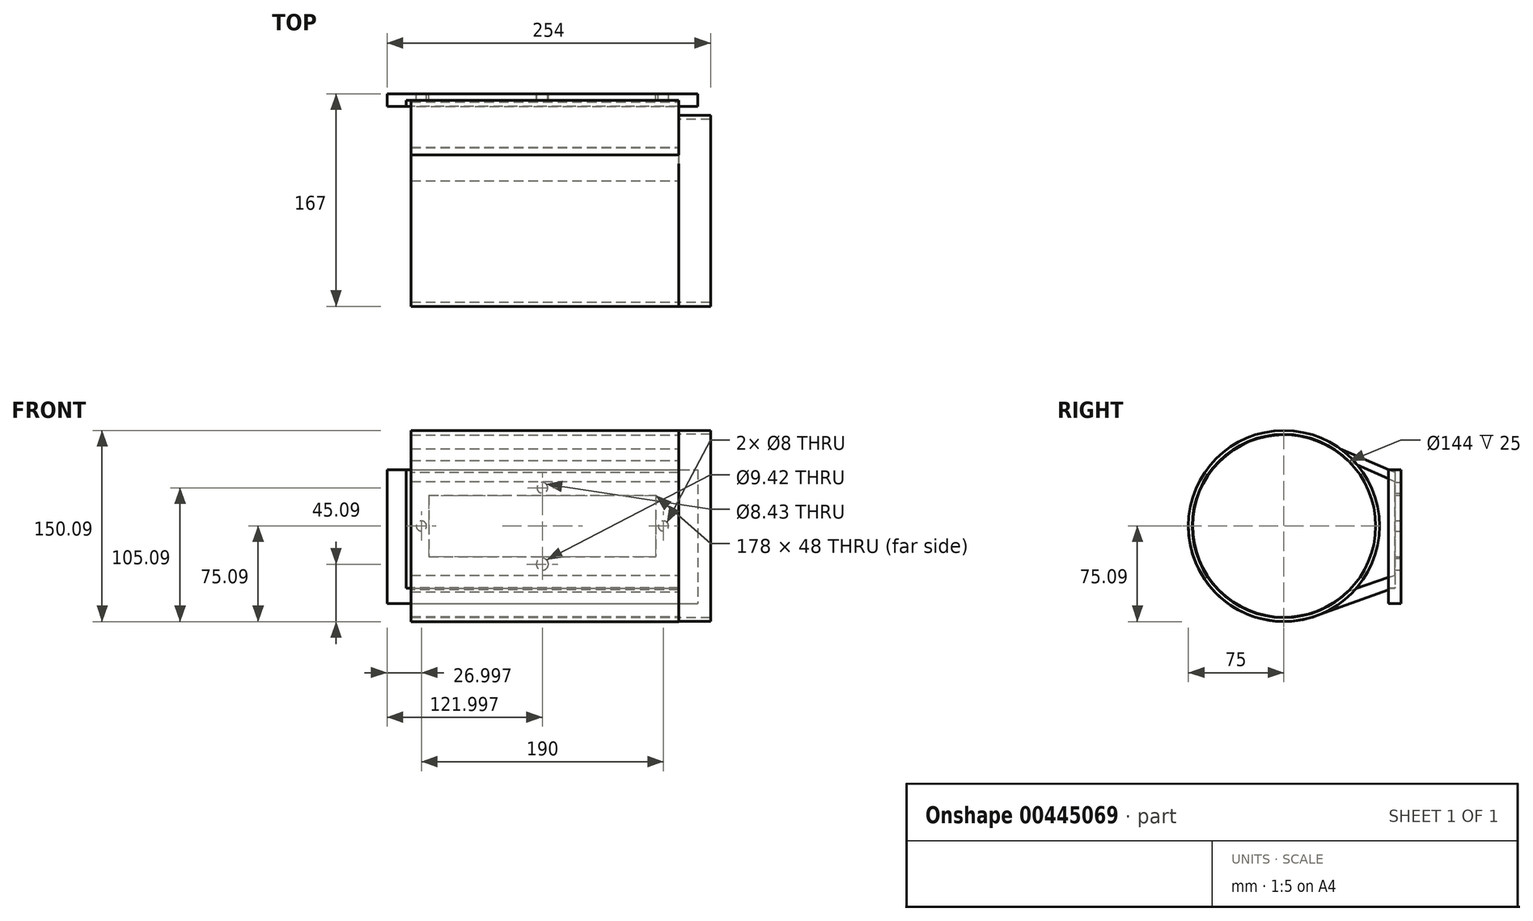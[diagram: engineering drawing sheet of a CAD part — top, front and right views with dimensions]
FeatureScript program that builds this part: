
annotation { "Feature Type Name" : "Feature", "Feature Type Description" : "" }
export const myFeature = defineFeature(function(context is Context, id is Id, definition is map)
    precondition{}
    {
        {
            var Q0;
            Q0=qCreatedBy(makeId("Front.planeOp"),FACE);
            var sketch = newSketch(context, id + "F0", { "sketchPlane" : qUnion([Q0])});
            skLineSegment(sketch, "E0.bottom", {"start": v(-132.21, 51.2) * mm, "end": v(45.79, 51.2) * mm});
            skLineSegment(sketch, "E0.top", {"start": v(-132.21, 3.2) * mm, "end": v(45.79, 3.2) * mm});
            skLineSegment(sketch, "E0.left", {"start": v(-132.21, 51.2) * mm, "end": v(-132.21, 3.2) * mm});
            skLineSegment(sketch, "E0.right", {"start": v(45.79, 51.2) * mm, "end": v(45.79, 3.2) * mm});
            skLineSegment(sketch, "E1.bottom", {"start": v(-165.21, 71.2) * mm, "end": v(78.79, 71.2) * mm});
            skLineSegment(sketch, "E1.top", {"start": v(-165.21, -33.8) * mm, "end": v(78.79, -33.8) * mm});
            skLineSegment(sketch, "E1.left", {"start": v(-165.21, 71.2) * mm, "end": v(-165.21, -33.8) * mm});
            skLineSegment(sketch, "E1.right", {"start": v(78.79, 71.2) * mm, "end": v(78.79, -33.8) * mm});
            skCircle(sketch, "E2", {"center": v(-138.21, 27.2) * mm, "radius": 4 * mm});
            skCircle(sketch, "E3", {"center": v(-43.21, 57.2) * mm, "radius": 4.21 * mm});
            skCircle(sketch, "E4", {"center": v(-43.21, -2.8) * mm, "radius": 4.7 * mm});
            skCircle(sketch, "E5", {"center": v(51.79, 27.2) * mm, "radius": 4 * mm});
            skLineSegment(sketch, "E6", {"start": v(-150.21, 71.2) * mm, "end": v(-150.21, -21.8) * mm});
            skLineSegment(sketch, "E7", {"start": v(-150.21, -21.8) * mm, "end": v(63.79, -21.8) * mm});
            skLineSegment(sketch, "E8", {"start": v(63.79, -21.8) * mm, "end": v(63.79, 71.2) * mm});
            skSolve(sketch);
        }
        {
            var Q0;
            Q0=makeQuery(id+"F0.imprint","IMPRINT",FACE,{"disambiguationData":[TD([[makeQuery(id+"F0.imprint","IMPRINT",EDGE,{"derivedFrom":sQuery(id+"F0.wireOp",EDGE,"E1.top")}),1.0]])]});
            extrude(context, id + "F1", {"entities" : qUnion([Q0]), "depth" : 10 * mm});
        }
        {
            var Q0;
            Q0=makeQuery(id+"F0.imprint","IMPRINT",FACE,{"disambiguationData":[TD([[makeQuery(id+"F0.imprint","IMPRINT",EDGE,{"derivedFrom":sQuery(id+"F0.wireOp",EDGE,"E0.bottom")}),1.0]])]});
            extrude(context, id + "F2", {"entities" : qUnion([Q0]), "operationType" : NewBodyOperationType.ADD, "depth" : 5 * mm});
        }
        {
            var Q0;
            Q0=makeQuery(id+"F1.opExtrude","SWEPT_FACE",FACE,{"disambiguationData":[OSD([sQuery(id+"F0.wireOp",EDGE,"E8")])]});
            cPlane(context, id + "F3", {"entities" : qUnion([Q0]), "cplaneType" : CPlaneType.OFFSET, "offset" : 0 * mm, "width" : 150 * mm, "height" : 150 * mm});
        }
        {
            var Q0;
            Q0=qCreatedBy(id+"F3.planeOp",FACE);
            var sketch = newSketch(context, id + "F4", { "sketchPlane" : qUnion([Q0])});
            skCircle(sketch, "E9", {"center": v(92, 27.2) * mm, "radius": 72 * mm});
            skCircle(sketch, "E10", {"center": v(92, 27.2) * mm, "radius": 75 * mm});
            skSolve(sketch);
        }
        {
            var Q0;
            Q0=makeQuery(id+"F4.imprint","IMPRINT",FACE,{"disambiguationData":[TD([[makeQuery(id+"F4.imprint","IMPRINT",EDGE,{"derivedFrom":sQuery(id+"F4.wireOp",EDGE,"E9")}),-1.0]])]});
            extrude(context, id + "F5", {"entities" : qUnion([Q0]), "oppositeDirection" : true, "depth" : 25 * mm, "offsetDistance" : 25 * mm});
        }
        {
            var Q0;
            Q0=makeQuery(id+"F2.opExtrude","CAP_FACE",FACE,{"disambiguationData":[OSD([sQuery(id+"F0.wireOp",EDGE,"E0.bottom"),sQuery(id+"F0.wireOp",EDGE,"E0.top"),sQuery(id+"F0.wireOp",EDGE,"E0.left"),sQuery(id+"F0.wireOp",EDGE,"E0.right"),sQuery(id+"F0.wireOp",EDGE,"E1.bottom"),sQuery(id+"F0.wireOp",EDGE,"E2"),sQuery(id+"F0.wireOp",EDGE,"E3"),sQuery(id+"F0.wireOp",EDGE,"E4"),sQuery(id+"F0.wireOp",EDGE,"E5"),sQuery(id+"F0.wireOp",EDGE,"E6"),sQuery(id+"F0.wireOp",EDGE,"E7"),sQuery(id+"F0.wireOp",EDGE,"E8")])],"isStart":false});
            var sketch = newSketch(context, id + "F6", { "sketchPlane" : qUnion([Q0])});
            skLineSegment(sketch, "E11.bottom", {"start": v(-143.21, 62.2) * mm, "end": v(56.79, 62.2) * mm});
            skLineSegment(sketch, "E11.top", {"start": v(-143.21, -7.8) * mm, "end": v(56.79, -7.8) * mm});
            skLineSegment(sketch, "E11.left", {"start": v(-143.21, 62.2) * mm, "end": v(-143.21, -7.8) * mm});
            skLineSegment(sketch, "E11.right", {"start": v(56.79, 62.2) * mm, "end": v(56.79, -7.8) * mm});
            skLineSegment(sketch, "E12.bottom", {"start": v(-146.21, 65.2) * mm, "end": v(63.79, 65.2) * mm});
            skLineSegment(sketch, "E12.top", {"start": v(-146.21, -10.8) * mm, "end": v(63.79, -10.8) * mm});
            skLineSegment(sketch, "E12.left", {"start": v(-146.21, 65.2) * mm, "end": v(-146.21, -10.8) * mm});
            skLineSegment(sketch, "E12.right", {"start": v(63.79, 65.2) * mm, "end": v(63.79, -10.8) * mm});
            skPoint(sketch, "E13", {"position": v(-146.21, 27.2) * mm});
            skPoint(sketch, "E14", {"position": v(-143.21, 27.2) * mm});
            skPoint(sketch, "E15", {"position": v(63.79, 27.2) * mm});
            skPoint(sketch, "E16", {"position": v(56.79, 27.2) * mm});
            skSolve(sketch);
        }
        {
            var Q0;
            Q0=qCreatedBy(makeId("Top.planeOp"),FACE);
            var Q1;
            Q1=sQuery(id+"F6.wireOp",VERTEX,"E16");
            cPlane(context, id + "F7", {"entities" : qUnion([Q0, Q1]), "cplaneType" : CPlaneType.PLANE_POINT, "offset" : 25 * mm, "width" : 150 * mm, "height" : 150 * mm});
        }
        {
            var Q0;
            Q0=makeQuery(id+"F5.opExtrude","CAP_FACE",FACE,{"disambiguationData":[OSD([sQuery(id+"F4.wireOp",EDGE,"E9"),sQuery(id+"F4.wireOp",EDGE,"E10")])],"isStart":true});
            var sketch = newSketch(context, id + "F8", { "sketchPlane" : qUnion([Q0])});
            skArc(sketch, "E17", {"start": v(30.36, 69.92) * mm, "mid": v(17.01, 25.76) * mm, "end": v(32.05, -17.86) * mm});
            skArc(sketch, "E18", {"start": v(152.74, 71.2) * mm, "mid": v(91.22, 102.2) * mm, "end": v(30.36, 69.92) * mm});
            skArc(sketch, "E19", {"start": v(154.43, -14.37) * mm, "mid": v(166.99, 28.68) * mm, "end": v(152.74, 71.2) * mm});
            skArc(sketch, "E20", {"start": v(32.05, -17.86) * mm, "mid": v(94.14, -47.77) * mm, "end": v(154.43, -14.37) * mm});
            skArc(sketch, "E21", {"start": v(33.1, 68.6) * mm, "mid": v(20, 27.2) * mm, "end": v(33.1, -14.2) * mm});
            skArc(sketch, "E22", {"start": v(33.1, -14.2) * mm, "mid": v(92.93, -44.8) * mm, "end": v(151.96, -12.66) * mm});
            skArc(sketch, "E23", {"start": v(151.96, -12.66) * mm, "mid": v(163.99, 28.46) * mm, "end": v(150.52, 69.14) * mm});
            skArc(sketch, "E24", {"start": v(150.52, 69.14) * mm, "mid": v(91.67, 99.2) * mm, "end": v(33.1, 68.6) * mm});
            skPoint(sketch, "E25", {"position": v(20, 27.2) * mm});
            skPoint(sketch, "E26", {"position": v(17, 27.2) * mm});
            skPoint(sketch, "E27", {"position": v(164, 27.2) * mm});
            skPoint(sketch, "E28", {"position": v(167, 27.2) * mm});
            skSolve(sketch);
        }
        {
            var Q0;
            Q0=makeQuery(id+"F1.opExtrude","CAP_EDGE",EDGE,{"disambiguationData":[OSD([sQuery(id+"F0.wireOp",EDGE,"E8")])],"isStart":false});
            cPlane(context, id + "F9", {"entities" : qUnion([Q0]), "cplaneType" : CPlaneType.LINE_ANGLE, "offset" : 25 * mm, "angle" : 135 * degree, "width" : 150 * mm, "height" : 150 * mm});
        }
        {
            var Q0;
            Q0=makeQuery(id+"F8.imprint","IMPRINT",FACE,{"disambiguationData":[TD([[makeQuery(id+"F8.imprint","IMPRINT",EDGE,{"derivedFrom":sQuery(id+"F8.wireOp",EDGE,"E17")}),1.0]])]});
            var sketch = newSketch(context, id + "F10", { "sketchPlane" : qUnion([Q0])});
            skLineSegment(sketch, "E29", {"start": v(4.9, 69.1) * mm, "end": v(47.93, 87.9) * mm});
            skLineSegment(sketch, "E30", {"start": v(4.56, -21.08) * mm, "end": v(68.18, -44.02) * mm});
            skArc(sketch, "E31", {"start": v(68.18, -44.02) * mm, "mid": v(166.13, 38.53) * mm, "end": v(47.93, 87.9) * mm});
            skLineSegment(sketch, "E32", {"start": v(4.9, 69.1) * mm, "end": v(4.88, 62.03) * mm});
            skArc(sketch, "E33", {"start": v(42.26, -24.5) * mm, "mid": v(163.64, 27.34) * mm, "end": v(41.98, 78.51) * mm});
            skLineSegment(sketch, "E34", {"start": v(41.98, 78.51) * mm, "end": v(4.88, 62.03) * mm});
            skLineSegment(sketch, "E35", {"start": v(42.26, -24.5) * mm, "end": v(4.6, -11.24) * mm});
            skLineSegment(sketch, "E36.trimOffspring", {"start": v(4.6, -11.24) * mm, "end": v(4.56, -21.08) * mm});
            skSolve(sketch);
        }
        {
            var Q0;
            Q0 = qSketchRegion(id + "F10", true);
            extrude(context, id + "F11", {"entities" : qUnion([Q0]), "operationType" : NewBodyOperationType.ADD, "depth" : 210 * mm, "offsetDistance" : 25 * mm});
        }
    });
